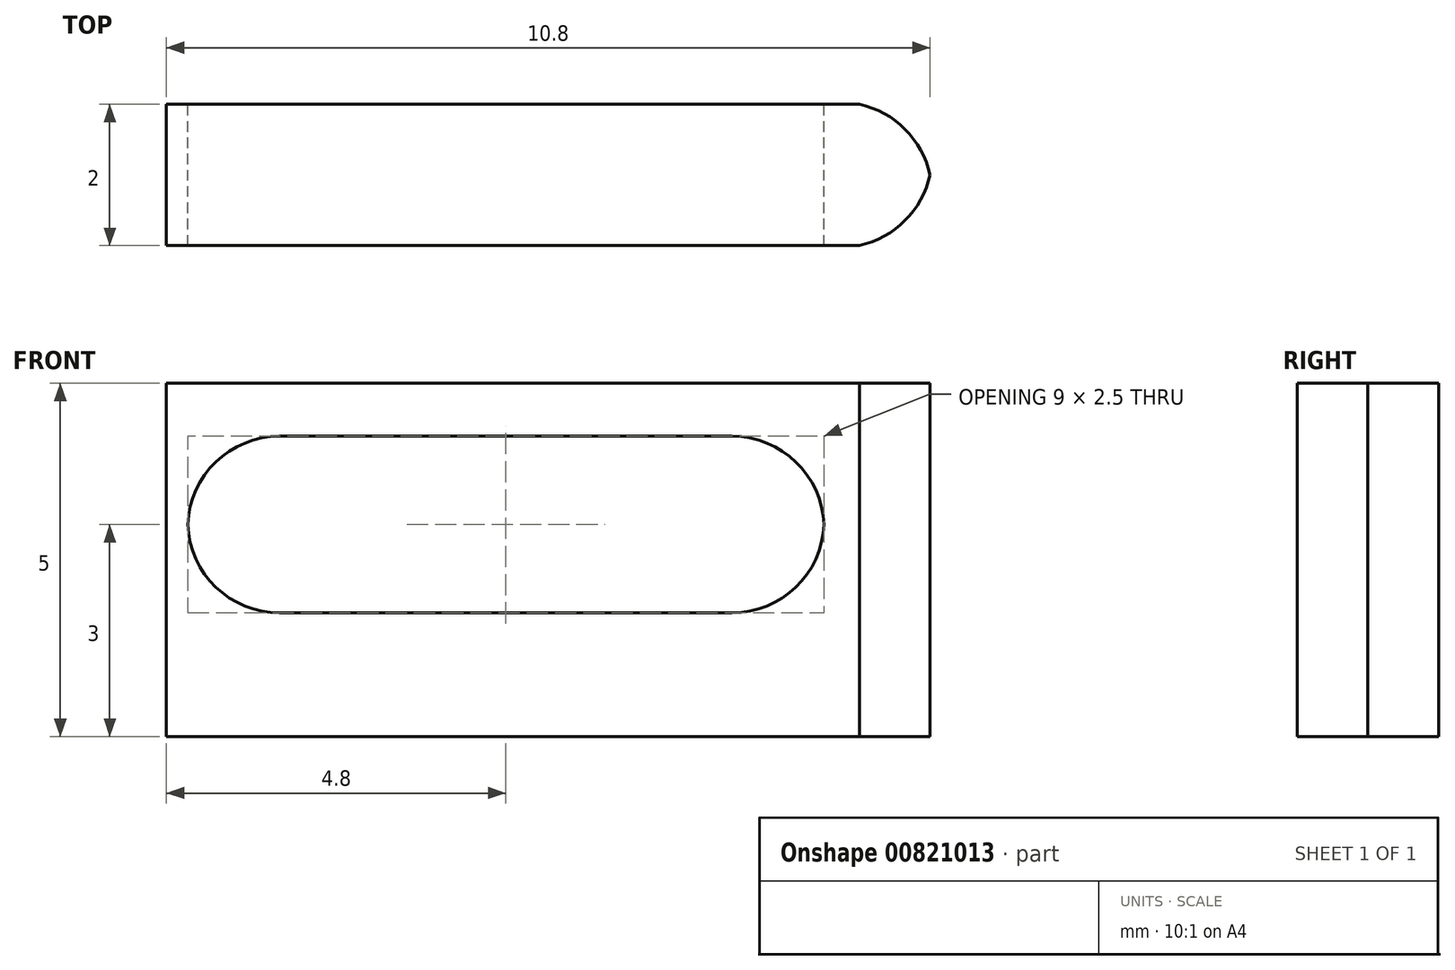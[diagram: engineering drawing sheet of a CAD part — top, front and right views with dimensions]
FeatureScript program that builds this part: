
annotation { "Feature Type Name" : "Feature", "Feature Type Description" : "" }
export const myFeature = defineFeature(function(context is Context, id is Id, definition is map)
    precondition{}
    {
        {
            var Q0;
            Q0=qCreatedBy(makeId("Top.planeOp"),FACE);
            var sketch = newSketch(context, id + "F0", { "sketchPlane" : qUnion([Q0])});
            skLineSegment(sketch, "E0.bottom", {"start": v(-6, 1) * mm, "end": v(6, 1) * mm});
            skLineSegment(sketch, "E0.top", {"start": v(-6, -1) * mm, "end": v(6, -1) * mm});
            skLineSegment(sketch, "E0.left", {"start": v(-6, 1) * mm, "end": v(-6, -1) * mm});
            skLineSegment(sketch, "E0.right", {"start": v(6, 1) * mm, "end": v(6, -1) * mm});
            skPoint(sketch, "E0.middle", {"position": v(0, 0) * mm});
            skArc(sketch, "E1", {"start": v(-6, 0) * mm, "mid": v(-5.65, -0.65) * mm, "end": v(-5, -1) * mm});
            skArc(sketch, "E2", {"start": v(-5, 1) * mm, "mid": v(-5.65, 0.65) * mm, "end": v(-6, 0) * mm});
            skArc(sketch, "E3", {"start": v(6, 0) * mm, "mid": v(5.65, 0.65) * mm, "end": v(5, 1) * mm});
            skArc(sketch, "E4", {"start": v(5, -1) * mm, "mid": v(5.65, -0.65) * mm, "end": v(6, 0) * mm});
            skSolve(sketch);
        }
        {
            var Q0;
            {var subQ0=sQuery(id+"F0.wireOp",EDGE,"E1");Q0=makeQuery(id+"F0.imprint","IMPRINT",FACE,{"disambiguationData":[TD([[makeQuery(id+"F0.imprint","IMPRINT",EDGE,{"derivedFrom":subQ0}),1.0]])]});}
            extrude(context, id + "F1", {"entities" : qUnion([Q0]), "depth" : 5 * mm, "offsetDistance" : 25 * mm});
        }
        {
            var Q0;
            Q0=makeQuery(id+"F1.opExtrude","SWEPT_FACE",FACE,{"disambiguationData":[OSD([sQuery(id+"F0.wireOp",EDGE,"E0.top")])]});
            var sketch = newSketch(context, id + "F2", { "sketchPlane" : qUnion([Q0])});
            skPoint(sketch, "E5", {"position": v(0, 3) * mm});
            skLineSegment(sketch, "E6.bottom", {"start": v(-4.5, 4.25) * mm, "end": v(4.5, 4.25) * mm});
            skLineSegment(sketch, "E6.top", {"start": v(-4.5, 1.75) * mm, "end": v(4.5, 1.75) * mm});
            skLineSegment(sketch, "E6.left", {"start": v(-4.5, 4.25) * mm, "end": v(-4.5, 1.75) * mm});
            skLineSegment(sketch, "E6.right", {"start": v(4.5, 4.25) * mm, "end": v(4.5, 1.75) * mm});
            skSolve(sketch);
        }
        {
            var Q0;
            Q0=makeQuery(id+"F2.imprint","IMPRINT",FACE,{"disambiguationData":[TD([[makeQuery(id+"F2.imprint","IMPRINT",EDGE,{"derivedFrom":sQuery(id+"F2.wireOp",EDGE,"E6.bottom")}),-1.0]])]});
            extrude(context, id + "F3", {"entities" : qUnion([Q0]), "operationType" : NewBodyOperationType.REMOVE, "endBound" : BoundingType.THROUGH_ALL, "oppositeDirection" : true, "depth" : 25 * mm, "offsetDistance" : 25 * mm});
        }
        {
            var Q0;
            Q0=makeQuery(id+"F3.boolean.opBoolean","COPY",EDGE,{"derivedFrom":makeQuery(id+"F3.opExtrude","SWEPT_EDGE",EDGE,{"disambiguationData":[OSD([sQuery(id+"F2.wireOp",EDGE,"E6.top"),sQuery(id+"F2.wireOp",EDGE,"E6.left")])]})});
            var Q1;
            Q1=makeQuery(id+"F3.boolean.opBoolean","COPY",EDGE,{"derivedFrom":makeQuery(id+"F3.opExtrude","SWEPT_EDGE",EDGE,{"disambiguationData":[OSD([sQuery(id+"F2.wireOp",EDGE,"E6.bottom"),sQuery(id+"F2.wireOp",EDGE,"E6.left")])]})});
            var Q2;
            Q2=makeQuery(id+"F3.boolean.opBoolean","COPY",EDGE,{"derivedFrom":makeQuery(id+"F3.opExtrude","SWEPT_EDGE",EDGE,{"disambiguationData":[OSD([sQuery(id+"F2.wireOp",EDGE,"E6.bottom"),sQuery(id+"F2.wireOp",EDGE,"E6.right")])]})});
            var Q3;
            Q3=makeQuery(id+"F3.boolean.opBoolean","COPY",EDGE,{"derivedFrom":makeQuery(id+"F3.opExtrude","SWEPT_EDGE",EDGE,{"disambiguationData":[OSD([sQuery(id+"F2.wireOp",EDGE,"E6.top"),sQuery(id+"F2.wireOp",EDGE,"E6.right")])]})});
            fillet(context, id + "F4", {"entities" : qUnion([Q0, Q1, Q2, Q3]), "radius" : 1.3 * mm, "tangentPropagation" : true, "allowEdgeOverflow" : false});
        }
        {
            var Q0;
            Q0=makeQuery(id+"F1.opExtrude","CAP_FACE",FACE,{"disambiguationData":[OSD([sQuery(id+"F0.wireOp",EDGE,"E0.bottom"),sQuery(id+"F0.wireOp",EDGE,"E0.top"),sQuery(id+"F0.wireOp",EDGE,"E1"),sQuery(id+"F0.wireOp",EDGE,"E2"),sQuery(id+"F0.wireOp",EDGE,"E3"),sQuery(id+"F0.wireOp",EDGE,"E4")])],"isStart":false});
            var sketch = newSketch(context, id + "F5", { "sketchPlane" : qUnion([Q0])});
            skLineSegment(sketch, "E7", {"start": v(-4.8, 1) * mm, "end": v(-4.8, -1) * mm});
            skSolve(sketch);
        }
        {
            var Q0;
            {var subQ3=sQuery(id+"F5.wireOp",EDGE,"E7");Q0=makeQuery(id+"F5.imprint","IMPRINT",FACE,{"disambiguationData":[TD([[makeQuery(id+"F5.imprint","IMPRINT",EDGE,{"derivedFrom":subQ3}),-1.0]])]});}
            extrude(context, id + "F6", {"entities" : qUnion([Q0]), "operationType" : NewBodyOperationType.REMOVE, "endBound" : BoundingType.THROUGH_ALL, "oppositeDirection" : true, "depth" : 25 * mm, "offsetDistance" : 25 * mm});
        }
    });
